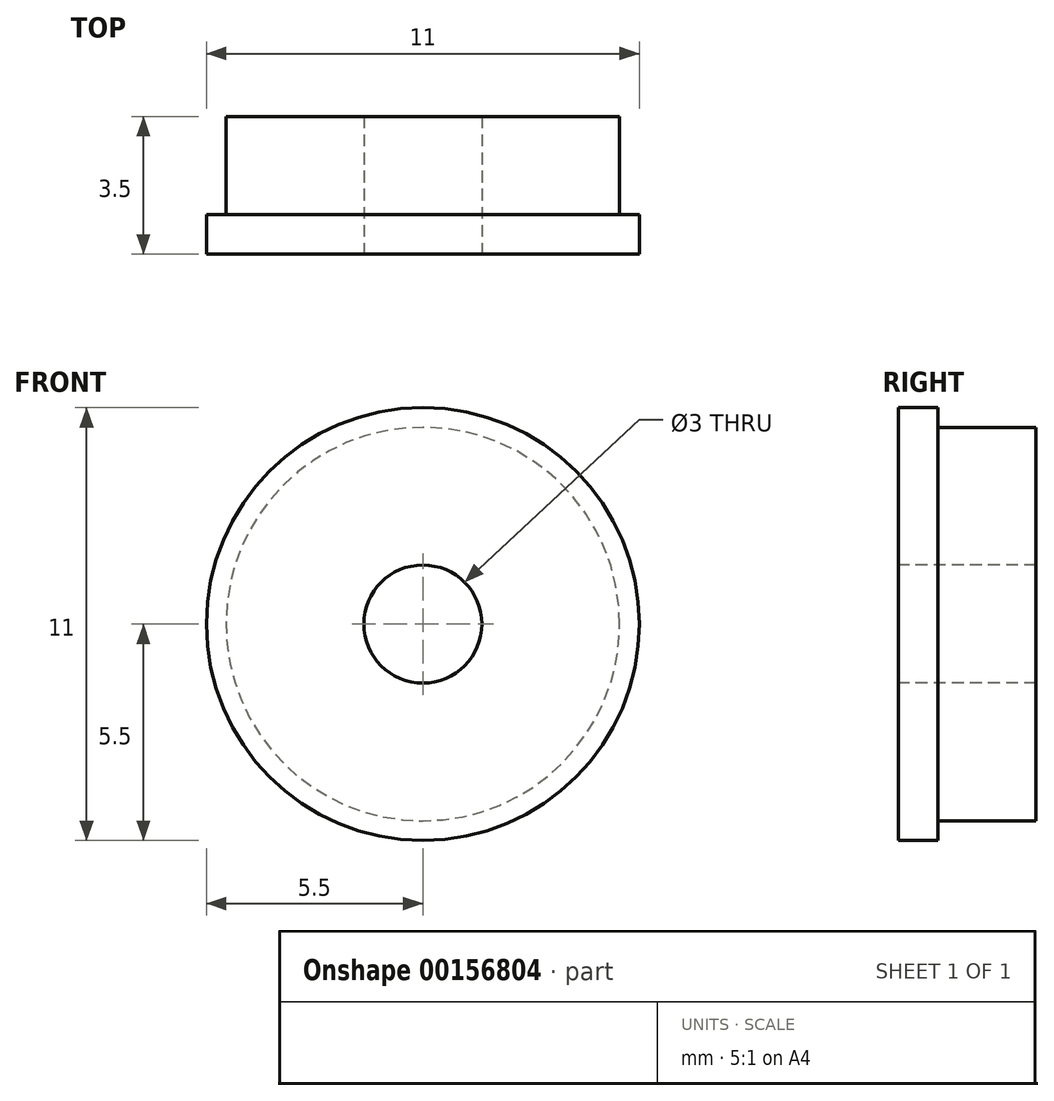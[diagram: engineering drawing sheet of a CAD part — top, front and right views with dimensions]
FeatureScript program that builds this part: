
annotation { "Feature Type Name" : "Feature", "Feature Type Description" : "" }
export const myFeature = defineFeature(function(context is Context, id is Id, definition is map)
    precondition{}
    {
        {
            var Q0;
            Q0=qCreatedBy(makeId("Top.planeOp"),FACE);
            var sketch = newSketch(context, id + "F0", { "sketchPlane" : qUnion([Q0])});
            skLineSegment(sketch, "E0", {"start": v(1.5, 0) * mm, "end": v(1.5, 3.5) * mm});
            skLineSegment(sketch, "E1", {"start": v(1.5, 3.5) * mm, "end": v(5, 3.5) * mm});
            skLineSegment(sketch, "E2", {"start": v(5, 3.5) * mm, "end": v(5, 1) * mm});
            skLineSegment(sketch, "E3", {"start": v(5, 1) * mm, "end": v(5.5, 1) * mm});
            skLineSegment(sketch, "E4", {"start": v(5.5, 1) * mm, "end": v(5.5, 0) * mm});
            skLineSegment(sketch, "E5", {"start": v(5.5, 0) * mm, "end": v(1.5, 0) * mm});
            skLineSegment(sketch, "E6", {"start": v(0, 0) * mm, "end": v(0, 3.48) * mm, "construction": true});
            skSolve(sketch);
        }
        {
            var Q0;
            Q0 = qSketchRegion(id + "F0", true);
            var Q1;
            Q1=sQuery(id+"F0.wireOp",EDGE,"E6");
            revolve(context, id + "F1", {"entities" : qUnion([Q0]), "axis" : qUnion([Q1]), "revolveType" : RevolveType.FULL});
        }
    });
